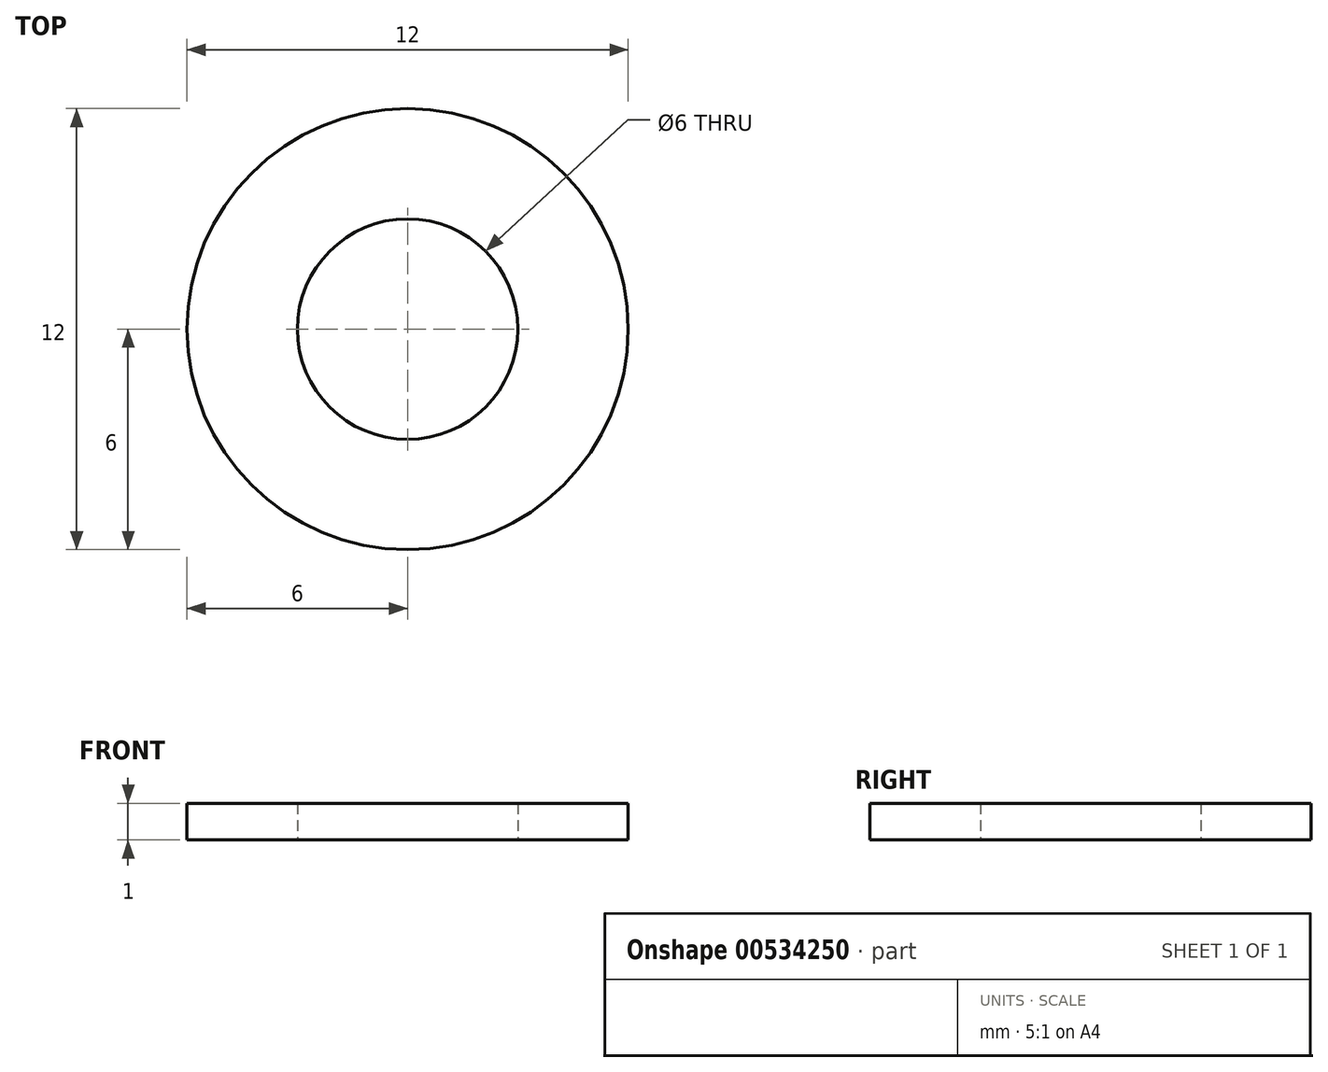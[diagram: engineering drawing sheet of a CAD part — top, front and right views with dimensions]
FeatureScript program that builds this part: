
annotation { "Feature Type Name" : "Feature", "Feature Type Description" : "" }
export const myFeature = defineFeature(function(context is Context, id is Id, definition is map)
    precondition{}
    {
        {
            var Q0;
            Q0=qCreatedBy(makeId("Front.planeOp"),FACE);
            var sketch = newSketch(context, id + "F0", { "sketchPlane" : qUnion([Q0])});
            skLineSegment(sketch, "E0.bottom", {"start": v(3, 0) * mm, "end": v(6, 0) * mm});
            skLineSegment(sketch, "E0.top", {"start": v(3, 1) * mm, "end": v(6, 1) * mm});
            skLineSegment(sketch, "E0.left", {"start": v(3, 0) * mm, "end": v(3, 1) * mm});
            skLineSegment(sketch, "E0.right", {"start": v(6, 0) * mm, "end": v(6, 1) * mm});
            skLineSegment(sketch, "E1", {"start": v(0, 0) * mm, "end": v(0, 8.17) * mm, "construction": true});
            skSolve(sketch);
        }
        {
            var Q0;
            Q0=makeQuery(id+"F0.imprint","IMPRINT",FACE,{"disambiguationData":[TD([[makeQuery(id+"F0.imprint","IMPRINT",EDGE,{"derivedFrom":sQuery(id+"F0.wireOp",EDGE,"E0.bottom")}),1.0]])]});
            var Q1;
            Q1=sQuery(id+"F0.wireOp",EDGE,"E1");
            revolve(context, id + "F1", {"entities" : qUnion([Q0]), "axis" : qUnion([Q1]), "revolveType" : RevolveType.FULL});
        }
    });
